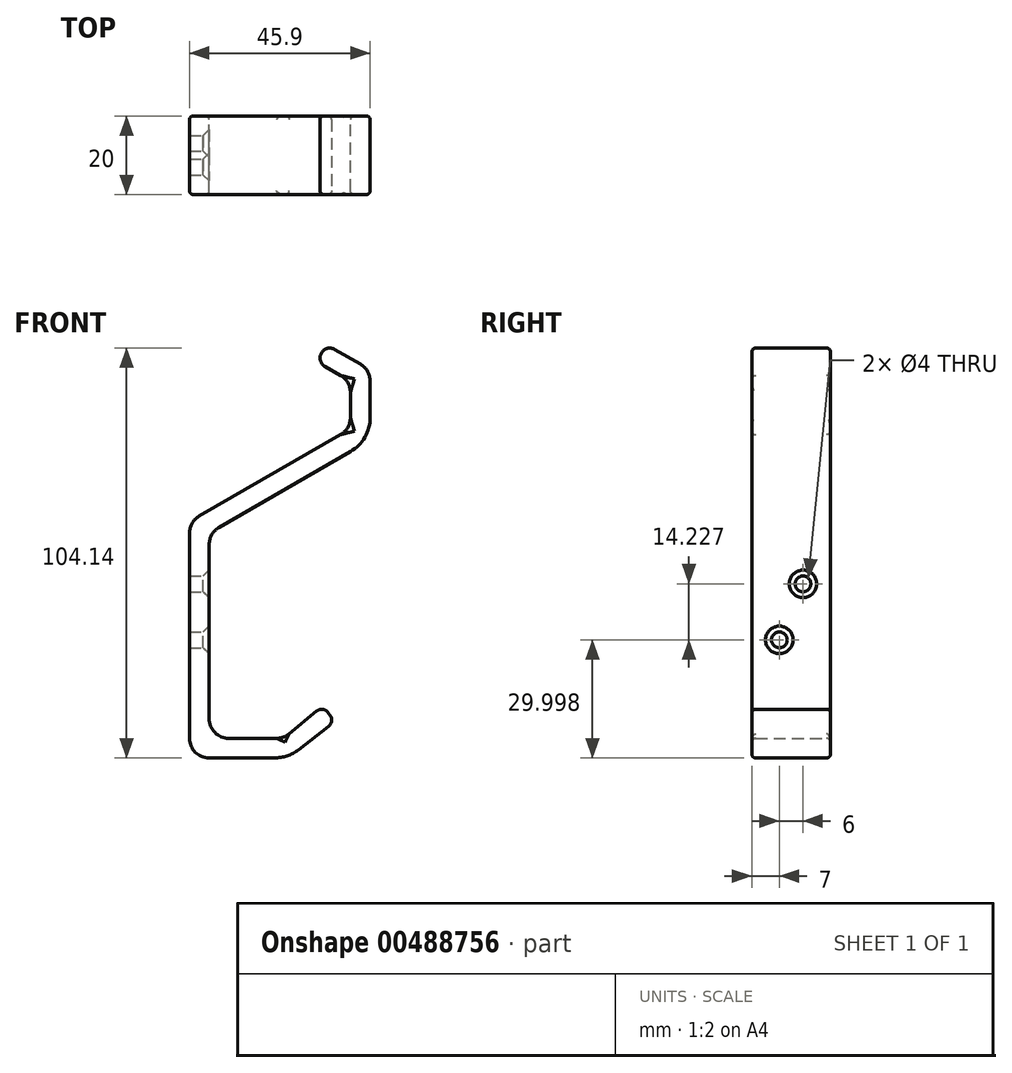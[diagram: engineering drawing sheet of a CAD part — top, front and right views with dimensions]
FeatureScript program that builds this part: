
annotation { "Feature Type Name" : "Feature", "Feature Type Description" : "" }
export const myFeature = defineFeature(function(context is Context, id is Id, definition is map)
    precondition{}
    {
        {
            var Q0;
            Q0=qCreatedBy(makeId("Front.planeOp"),FACE);
            var sketch = newSketch(context, id + "F0", { "sketchPlane" : qUnion([Q0])});
            skLineSegment(sketch, "E0", {"start": v(-34.74, 60.63) * mm, "end": v(-34.74, 0.63) * mm});
            skLineSegment(sketch, "E1", {"start": v(-34.74, 0.63) * mm, "end": v(-9.74, 0.63) * mm});
            skLineSegment(sketch, "E2", {"start": v(-9.74, 0.63) * mm, "end": v(2.12, 9.81) * mm});
            skLineSegment(sketch, "E3", {"start": v(11.16, 81.36) * mm, "end": v(-29.74, 57.74) * mm});
            skLineSegment(sketch, "E4", {"start": v(-29.74, 57.74) * mm, "end": v(-29.74, 5.63) * mm});
            skLineSegment(sketch, "E5", {"start": v(-29.74, 5.63) * mm, "end": v(-10.8, 5.63) * mm});
            skLineSegment(sketch, "E6", {"start": v(-10.8, 5.63) * mm, "end": v(-0.74, 13.92) * mm});
            skLineSegment(sketch, "E7", {"start": v(-0.74, 13.92) * mm, "end": v(2.12, 9.81) * mm});
            skLineSegment(sketch, "E8", {"start": v(6.16, 96.36) * mm, "end": v(6.16, 84.24) * mm});
            skLineSegment(sketch, "E9", {"start": v(6.16, 84.24) * mm, "end": v(-34.74, 60.63) * mm});
            skLineSegment(sketch, "E10", {"start": v(6.16, 96.36) * mm, "end": v(-2.5, 101.36) * mm});
            skLineSegment(sketch, "E11", {"start": v(-2.5, 101.36) * mm, "end": v(0, 105.69) * mm});
            skLineSegment(sketch, "E12", {"start": v(0, 105.69) * mm, "end": v(11.16, 99.24) * mm});
            skLineSegment(sketch, "E13", {"start": v(11.16, 99.24) * mm, "end": v(11.16, 81.36) * mm});
            skSolve(sketch);
        }
        {
            var Q0;
            Q0=makeQuery(id+"F0.imprint","IMPRINT",FACE,{"disambiguationData":[TD([[makeQuery(id+"F0.imprint","IMPRINT",EDGE,{"derivedFrom":sQuery(id+"F0.wireOp",EDGE,"E0")}),1.0]])]});
            extrude(context, id + "F1", {"entities" : qUnion([Q0]), "depth" : 20 * mm, "offsetDistance" : 25 * mm});
        }
        {
            var Q0;
            Q0=makeQuery(id+"F1.opExtrude","SWEPT_EDGE",EDGE,{"disambiguationData":[OSD([sQuery(id+"F0.wireOp",EDGE,"E3"),sQuery(id+"F0.wireOp",EDGE,"E4")])]});
            fillet(context, id + "F2", {"entities" : qUnion([Q0]), "radius" : 5 * mm, "tangentPropagation" : true, "allowEdgeOverflow" : false});
        }
        {
            var Q0;
            Q0=makeQuery(id+"F1.opExtrude","SWEPT_EDGE",EDGE,{"disambiguationData":[OSD([sQuery(id+"F0.wireOp",EDGE,"E0"),sQuery(id+"F0.wireOp",EDGE,"aPAtAyns-X2Dq-PHJm-WIcm-KSb39C0CfUOW")])]});
            fillet(context, id + "F3", {"entities" : qUnion([Q0]), "radius" : 5 * mm, "tangentPropagation" : true, "allowEdgeOverflow" : false});
        }
        {
            var Q0;
            Q0=makeQuery(id+"F1.opExtrude","SWEPT_EDGE",EDGE,{"disambiguationData":[OSD([sQuery(id+"F0.wireOp",EDGE,"E6"),sQuery(id+"F0.wireOp",EDGE,"E7")])]});
            fillet(context, id + "F4", {"entities" : qUnion([Q0]), "radius" : 2 * mm, "tangentPropagation" : true, "allowEdgeOverflow" : false});
        }
        {
            var Q0;
            Q0=makeQuery(id+"F1.opExtrude","SWEPT_EDGE",EDGE,{"disambiguationData":[OSD([sQuery(id+"F0.wireOp",EDGE,"E2"),sQuery(id+"F0.wireOp",EDGE,"E7")])]});
            fillet(context, id + "F5", {"entities" : qUnion([Q0]), "radius" : 2 * mm, "tangentPropagation" : true, "allowEdgeOverflow" : false});
        }
        {
            var Q0;
            Q0=makeQuery(id+"F1.opExtrude","SWEPT_EDGE",EDGE,{"disambiguationData":[OSD([sQuery(id+"F0.wireOp",EDGE,"E4"),sQuery(id+"F0.wireOp",EDGE,"E5")])]});
            fillet(context, id + "F6", {"entities" : qUnion([Q0]), "radius" : 5 * mm, "tangentPropagation" : true, "allowEdgeOverflow" : false});
        }
        {
            var Q0;
            Q0=makeQuery(id+"F1.opExtrude","CAP_FACE",FACE,{"disambiguationData":[OSD([sQuery(id+"F0.wireOp",EDGE,"E0"),sQuery(id+"F0.wireOp",EDGE,"E1"),sQuery(id+"F0.wireOp",EDGE,"aPAtAyns-X2Dq-PHJm-WIcm-KSb39C0CfUOW"),sQuery(id+"F0.wireOp",EDGE,"E2"),sQuery(id+"F0.wireOp",EDGE,"htOgHLCZ-kXDS-aOfo-sJgo-odmLCGzegei1"),sQuery(id+"F0.wireOp",EDGE,"E3"),sQuery(id+"F0.wireOp",EDGE,"E4"),sQuery(id+"F0.wireOp",EDGE,"E5"),sQuery(id+"F0.wireOp",EDGE,"E6"),sQuery(id+"F0.wireOp",EDGE,"E7")])],"isStart":false});
            fillet(context, id + "F7", {"entities" : qUnion([Q0]), "radius" : 1 * mm, "tangentPropagation" : true, "allowEdgeOverflow" : false});
        }
        {
            var Q0;
            Q0=makeQuery(id+"F1.opExtrude","CAP_FACE",FACE,{"disambiguationData":[OSD([sQuery(id+"F0.wireOp",EDGE,"E0"),sQuery(id+"F0.wireOp",EDGE,"E1"),sQuery(id+"F0.wireOp",EDGE,"aPAtAyns-X2Dq-PHJm-WIcm-KSb39C0CfUOW"),sQuery(id+"F0.wireOp",EDGE,"E2"),sQuery(id+"F0.wireOp",EDGE,"htOgHLCZ-kXDS-aOfo-sJgo-odmLCGzegei1"),sQuery(id+"F0.wireOp",EDGE,"E3"),sQuery(id+"F0.wireOp",EDGE,"E4"),sQuery(id+"F0.wireOp",EDGE,"E5"),sQuery(id+"F0.wireOp",EDGE,"E6"),sQuery(id+"F0.wireOp",EDGE,"E7")])],"isStart":true});
            fillet(context, id + "F8", {"entities" : qUnion([Q0]), "radius" : 1 * mm, "tangentPropagation" : true, "allowEdgeOverflow" : false});
        }
        {
            var Q0;
            Q0=makeQuery(id+"F1.opExtrude","SWEPT_EDGE",EDGE,{"disambiguationData":[OSD([sQuery(id+"F0.wireOp",EDGE,"E1"),sQuery(id+"F0.wireOp",EDGE,"E2")])]});
            fillet(context, id + "F9", {"entities" : qUnion([Q0]), "radius" : 10 * mm, "tangentPropagation" : true, "allowEdgeOverflow" : false});
        }
        {
            var Q0;
            Q0=makeQuery(id+"F1.opExtrude","SWEPT_EDGE",EDGE,{"disambiguationData":[OSD([sQuery(id+"F0.wireOp",EDGE,"E5"),sQuery(id+"F0.wireOp",EDGE,"E6")])]});
            fillet(context, id + "F10", {"entities" : qUnion([Q0]), "radius" : 5 * mm, "tangentPropagation" : true, "allowEdgeOverflow" : false});
        }
        {
            var Q0;
            Q0=makeQuery(id+"F1.opExtrude","SWEPT_FACE",FACE,{"disambiguationData":[OSD([sQuery(id+"F0.wireOp",EDGE,"E4")])]});
            var sketch = newSketch(context, id + "F11", { "sketchPlane" : qUnion([Q0])});
            skPoint(sketch, "E14", {"position": v(-7, 44.85) * mm});
            skPoint(sketch, "E15", {"position": v(-13, 30.63) * mm});
            skSolve(sketch);
        }
        {
            var Q0;
            Q0=sQuery(id+"F11.wireOp",VERTEX,"E14");
            var Q1;
            Q1=sQuery(id+"F11.wireOp",VERTEX,"E15");
            var Q2;
            Q2=makeQuery(id+"F1.opExtrude","SWEPT_BODY",BODY,{"disambiguationData":[OSD([sQuery(id+"F0.wireOp",EDGE,"E0"),sQuery(id+"F0.wireOp",EDGE,"E1"),sQuery(id+"F0.wireOp",EDGE,"aPAtAyns-X2Dq-PHJm-WIcm-KSb39C0CfUOW"),sQuery(id+"F0.wireOp",EDGE,"E2"),sQuery(id+"F0.wireOp",EDGE,"htOgHLCZ-kXDS-aOfo-sJgo-odmLCGzegei1"),sQuery(id+"F0.wireOp",EDGE,"E3"),sQuery(id+"F0.wireOp",EDGE,"E4"),sQuery(id+"F0.wireOp",EDGE,"E5"),sQuery(id+"F0.wireOp",EDGE,"E6"),sQuery(id+"F0.wireOp",EDGE,"E7")])]});
            hole(context, id + "F12", {"style" : HoleStyle.C_SINK, "endStyle" : HoleEndStyle.THROUGH, "holeDiameter" : 4 * mm, "cSinkDiameter" : 7 * mm, "cSinkAngle" : 90 * degree, "majorDiameter" : 5 * mm, "isTappedThrough" : true, "tappedDepth" : 12 * mm, "tapClearance" : 3, "locations" : qUnion([Q0, Q1]), "scope" : qUnion([Q2])});
        }
        {
            var Q0;
            Q0=makeQuery(id+"F1.opExtrude","SWEPT_EDGE",EDGE,{"disambiguationData":[OSD([sQuery(id+"F0.wireOp",EDGE,"E8"),sQuery(id+"F0.wireOp",EDGE,"E9")])]});
            fillet(context, id + "F13", {"entities" : qUnion([Q0]), "radius" : 5 * mm, "tangentPropagation" : true, "allowEdgeOverflow" : false});
        }
        {
            var Q0;
            Q0=makeQuery(id+"F1.opExtrude","SWEPT_EDGE",EDGE,{"disambiguationData":[OSD([sQuery(id+"F0.wireOp",EDGE,"E12"),sQuery(id+"F0.wireOp",EDGE,"E13")])]});
            fillet(context, id + "F14", {"entities" : qUnion([Q0]), "radius" : 5 * mm, "tangentPropagation" : true, "allowEdgeOverflow" : false});
        }
        {
            var Q0;
            Q0=makeQuery(id+"F1.opExtrude","SWEPT_EDGE",EDGE,{"disambiguationData":[OSD([sQuery(id+"F0.wireOp",EDGE,"E3"),sQuery(id+"F0.wireOp",EDGE,"E13")])]});
            fillet(context, id + "F15", {"entities" : qUnion([Q0]), "radius" : 10 * mm, "tangentPropagation" : true, "allowEdgeOverflow" : false});
        }
        {
            var Q0;
            Q0=makeQuery(id+"F1.opExtrude","SWEPT_EDGE",EDGE,{"disambiguationData":[OSD([sQuery(id+"F0.wireOp",EDGE,"E8"),sQuery(id+"F0.wireOp",EDGE,"E10")])]});
            fillet(context, id + "F16", {"entities" : qUnion([Q0]), "radius" : 5 * mm, "tangentPropagation" : true, "allowEdgeOverflow" : false});
        }
        {
            var Q0;
            Q0=makeQuery(id+"F1.opExtrude","SWEPT_EDGE",EDGE,{"disambiguationData":[OSD([sQuery(id+"F0.wireOp",EDGE,"E11"),sQuery(id+"F0.wireOp",EDGE,"E12")])]});
            fillet(context, id + "F17", {"entities" : qUnion([Q0]), "radius" : 2.5 * mm, "tangentPropagation" : true, "allowEdgeOverflow" : false});
        }
        {
            var Q0;
            Q0=makeQuery(id+"F1.opExtrude","SWEPT_EDGE",EDGE,{"disambiguationData":[OSD([sQuery(id+"F0.wireOp",EDGE,"E10"),sQuery(id+"F0.wireOp",EDGE,"E11")])]});
            fillet(context, id + "F18", {"entities" : qUnion([Q0]), "radius" : 2.5 * mm, "tangentPropagation" : true, "allowEdgeOverflow" : false});
        }
    });
